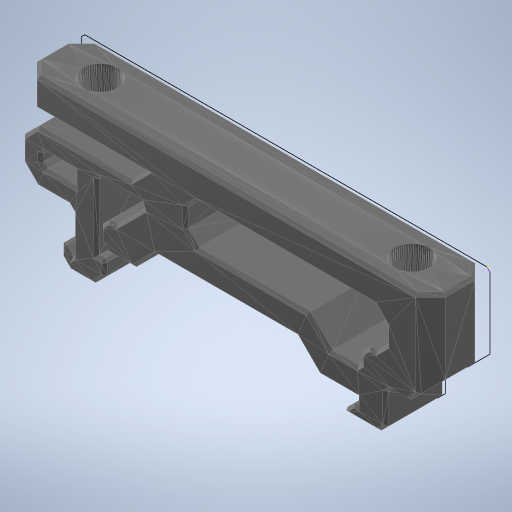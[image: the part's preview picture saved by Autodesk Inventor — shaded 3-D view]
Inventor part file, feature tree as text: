
AUTODESK INVENTOR PART (.ipt)
format: ipt  version: 2023 (Build 270158000, 158)  size: 316,928 bytes
history: native  units: in
note: dims shown in document units (in); Inventor stores cm internally (conversion verified against a paired STEP export)
features: other x2, sketch x1
ambient origin geometry x8: Origin, YZ Plane, XZ Plane, XY Plane, X Axis, Y Axis, Z Axis, Center Point
feature tree (3):
  other  "UHP_200_Mount_x2 (1)"
  sketch  "Sketch1"
  other  "MeshFeature1"
